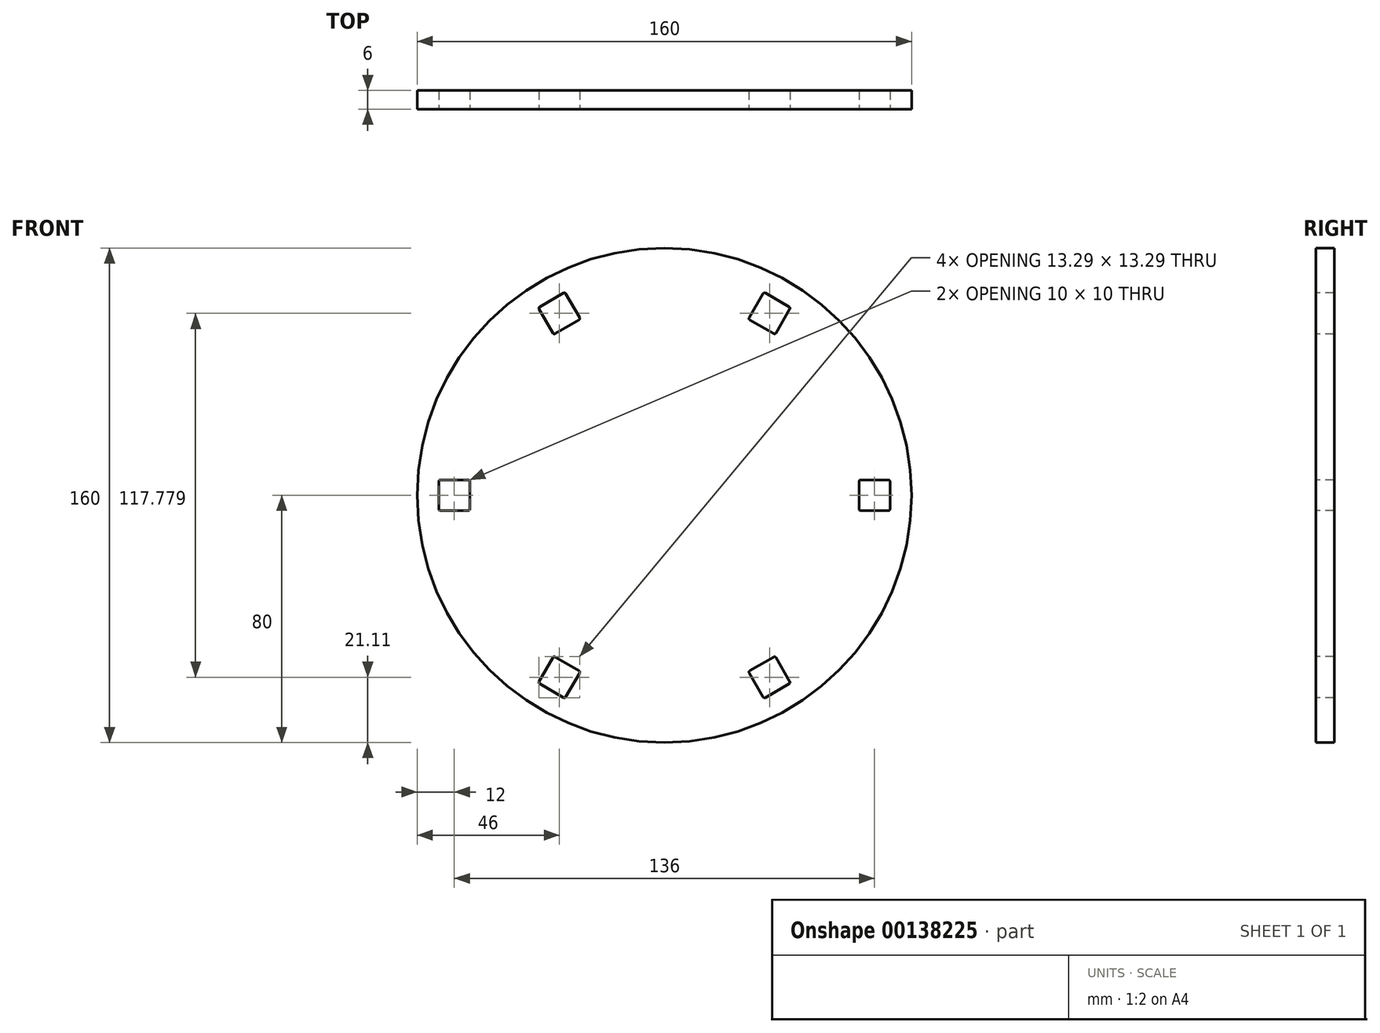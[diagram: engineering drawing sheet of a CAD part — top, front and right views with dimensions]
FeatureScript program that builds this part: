
annotation { "Feature Type Name" : "Feature", "Feature Type Description" : "" }
export const myFeature = defineFeature(function(context is Context, id is Id, definition is map)
    precondition{}
    {
        {
            var Q0;
            Q0=qCreatedBy(makeId("Front.planeOp"),FACE);
            var sketch = newSketch(context, id + "F0", { "sketchPlane" : qUnion([Q0])});
            skCircle(sketch, "E0", {"center": v(0, 0) * mm, "radius": 80 * mm});
            skCircle(sketch, "E1", {"center": v(0, 0) * mm, "radius": 56 * mm, "construction": true});
            skLineSegment(sketch, "E2", {"start": v(0, 80) * mm, "end": v(0, 56) * mm, "construction": true});
            skPoint(sketch, "E3", {"position": v(0, 68) * mm});
            skCircle(sketch, "E4", {"center": v(0, 0) * mm, "radius": 68 * mm, "construction": true});
            skLineSegment(sketch, "E5", {"start": v(-34, 58.89) * mm, "end": v(34, 58.89) * mm, "construction": true});
            skLineSegment(sketch, "E6", {"start": v(34, 58.89) * mm, "end": v(68, 0) * mm, "construction": true});
            skLineSegment(sketch, "E7", {"start": v(68, 0) * mm, "end": v(34, -58.89) * mm, "construction": true});
            skLineSegment(sketch, "E8", {"start": v(34, -58.89) * mm, "end": v(-34, -58.89) * mm, "construction": true});
            skLineSegment(sketch, "E9", {"start": v(-34, -58.89) * mm, "end": v(-68, 0) * mm, "construction": true});
            skLineSegment(sketch, "E10", {"start": v(-68, 0) * mm, "end": v(-34, 58.89) * mm, "construction": true});
            skSolve(sketch);
        }
        {
            var Q0;
            Q0 = qSketchRegion(id + "F0", true);
            extrude(context, id + "F1", {"entities" : qUnion([Q0]), "depth" : 6 * mm});
        }
        {
            var Q0;
            Q0=makeQuery(id+"F1.opExtrude","CAP_FACE",FACE,{"disambiguationData":[OSD([sQuery(id+"F0.wireOp",EDGE,"E0")])],"isStart":false});
            var sketch = newSketch(context, id + "F2", { "sketchPlane" : qUnion([Q0])});
            skLineSegment(sketch, "E11.bottom", {"start": v(-72.5, 5) * mm, "end": v(-63.5, 5) * mm});
            skLineSegment(sketch, "E11.top", {"start": v(-72.5, -5) * mm, "end": v(-63.5, -5) * mm});
            skLineSegment(sketch, "E11.left", {"start": v(-73, 4.5) * mm, "end": v(-73, -4.5) * mm});
            skLineSegment(sketch, "E11.right", {"start": v(-63, 4.5) * mm, "end": v(-63, -4.5) * mm});
            skLineSegment(sketch, "E12", {"start": v(-73, -5) * mm, "end": v(-63, 5) * mm, "construction": true});
            skLineSegment(sketch, "E13", {"start": v(-63, -5) * mm, "end": v(-73, 5) * mm, "construction": true});
            skPoint(sketch, "E14.visualSharp", {"position": v(-73, 5) * mm});
            skArc(sketch, "E14.filletArc", {"start": v(-72.5, 5) * mm, "mid": v(-72.85, 4.85) * mm, "end": v(-73, 4.5) * mm});
            skPoint(sketch, "E15.visualSharp", {"position": v(-63, 5) * mm});
            skArc(sketch, "E15.filletArc", {"start": v(-63, 4.5) * mm, "mid": v(-63.15, 4.85) * mm, "end": v(-63.5, 5) * mm});
            skPoint(sketch, "E16.visualSharp", {"position": v(-63, -5) * mm});
            skArc(sketch, "E16.filletArc", {"start": v(-63.5, -5) * mm, "mid": v(-63.15, -4.85) * mm, "end": v(-63, -4.5) * mm});
            skPoint(sketch, "E17.visualSharp", {"position": v(-73, -5) * mm});
            skArc(sketch, "E17.filletArc", {"start": v(-73, -4.5) * mm, "mid": v(-72.85, -4.85) * mm, "end": v(-72.5, -5) * mm});
            skLineSegment(sketch, "E18.1.0", {"start": v(-31.92, -65.29) * mm, "end": v(-27.42, -57.5) * mm});
            skPoint(sketch, "E18.1.1", {"position": v(-35.83, -52.06) * mm});
            skLineSegment(sketch, "E18.1.2", {"start": v(-40.4, -60.97) * mm, "end": v(-32.6, -65.47) * mm});
            skLineSegment(sketch, "E18.1.3", {"start": v(-40.58, -60.29) * mm, "end": v(-36.08, -52.5) * mm});
            skPoint(sketch, "E18.1.4", {"position": v(-40.83, -60.72) * mm});
            skPoint(sketch, "E18.1.5", {"position": v(-32.17, -65.72) * mm});
            skPoint(sketch, "E18.1.6", {"position": v(-27.17, -57.06) * mm});
            skLineSegment(sketch, "E18.1.7", {"start": v(-35.4, -52.3) * mm, "end": v(-27.6, -56.8) * mm});
            skLineSegment(sketch, "E18.1.8", {"start": v(-32.17, -65.72) * mm, "end": v(-35.83, -52.06) * mm, "construction": true});
            skLineSegment(sketch, "E18.1.9", {"start": v(-27.17, -57.06) * mm, "end": v(-40.83, -60.72) * mm, "construction": true});
            skArc(sketch, "E18.1.10", {"start": v(-32.6, -65.47) * mm, "mid": v(-32.22, -65.52) * mm, "end": v(-31.92, -65.29) * mm});
            skArc(sketch, "E18.1.11", {"start": v(-27.42, -57.5) * mm, "mid": v(-27.37, -57.11) * mm, "end": v(-27.6, -56.8) * mm});
            skArc(sketch, "E18.1.12", {"start": v(-35.4, -52.3) * mm, "mid": v(-35.78, -52.26) * mm, "end": v(-36.08, -52.5) * mm});
            skArc(sketch, "E18.1.13", {"start": v(-40.58, -60.29) * mm, "mid": v(-40.63, -60.67) * mm, "end": v(-40.4, -60.97) * mm});
            skLineSegment(sketch, "E18.2.0", {"start": v(40.58, -60.29) * mm, "end": v(36.08, -52.5) * mm});
            skPoint(sketch, "E18.2.1", {"position": v(27.17, -57.06) * mm});
            skLineSegment(sketch, "E18.2.2", {"start": v(32.6, -65.47) * mm, "end": v(40.4, -60.97) * mm});
            skLineSegment(sketch, "E18.2.3", {"start": v(31.92, -65.29) * mm, "end": v(27.42, -57.5) * mm});
            skPoint(sketch, "E18.2.4", {"position": v(32.17, -65.72) * mm});
            skPoint(sketch, "E18.2.5", {"position": v(40.83, -60.72) * mm});
            skPoint(sketch, "E18.2.6", {"position": v(35.83, -52.06) * mm});
            skLineSegment(sketch, "E18.2.7", {"start": v(27.6, -56.8) * mm, "end": v(35.4, -52.3) * mm});
            skLineSegment(sketch, "E18.2.8", {"start": v(40.83, -60.72) * mm, "end": v(27.17, -57.06) * mm, "construction": true});
            skLineSegment(sketch, "E18.2.9", {"start": v(35.83, -52.06) * mm, "end": v(32.17, -65.72) * mm, "construction": true});
            skArc(sketch, "E18.2.10", {"start": v(40.4, -60.97) * mm, "mid": v(40.63, -60.67) * mm, "end": v(40.58, -60.29) * mm});
            skArc(sketch, "E18.2.11", {"start": v(36.08, -52.5) * mm, "mid": v(35.78, -52.26) * mm, "end": v(35.4, -52.3) * mm});
            skArc(sketch, "E18.2.12", {"start": v(27.6, -56.8) * mm, "mid": v(27.37, -57.11) * mm, "end": v(27.42, -57.5) * mm});
            skArc(sketch, "E18.2.13", {"start": v(31.92, -65.29) * mm, "mid": v(32.22, -65.52) * mm, "end": v(32.6, -65.47) * mm});
            skLineSegment(sketch, "E18.3.0", {"start": v(72.5, 5) * mm, "end": v(63.5, 5) * mm});
            skPoint(sketch, "E18.3.1", {"position": v(63, -5) * mm});
            skLineSegment(sketch, "E18.3.2", {"start": v(73, -4.5) * mm, "end": v(73, 4.5) * mm});
            skLineSegment(sketch, "E18.3.3", {"start": v(72.5, -5) * mm, "end": v(63.5, -5) * mm});
            skPoint(sketch, "E18.3.4", {"position": v(73, -5) * mm});
            skPoint(sketch, "E18.3.5", {"position": v(73, 5) * mm});
            skPoint(sketch, "E18.3.6", {"position": v(63, 5) * mm});
            skLineSegment(sketch, "E18.3.7", {"start": v(63, -4.5) * mm, "end": v(63, 4.5) * mm});
            skLineSegment(sketch, "E18.3.8", {"start": v(73, 5) * mm, "end": v(63, -5) * mm, "construction": true});
            skLineSegment(sketch, "E18.3.9", {"start": v(63, 5) * mm, "end": v(73, -5) * mm, "construction": true});
            skArc(sketch, "E18.3.10", {"start": v(73, 4.5) * mm, "mid": v(72.85, 4.85) * mm, "end": v(72.5, 5) * mm});
            skArc(sketch, "E18.3.11", {"start": v(63.5, 5) * mm, "mid": v(63.15, 4.85) * mm, "end": v(63, 4.5) * mm});
            skArc(sketch, "E18.3.12", {"start": v(63, -4.5) * mm, "mid": v(63.15, -4.85) * mm, "end": v(63.5, -5) * mm});
            skArc(sketch, "E18.3.13", {"start": v(72.5, -5) * mm, "mid": v(72.85, -4.85) * mm, "end": v(73, -4.5) * mm});
            skLineSegment(sketch, "E18.4.0", {"start": v(31.92, 65.29) * mm, "end": v(27.42, 57.5) * mm});
            skPoint(sketch, "E18.4.1", {"position": v(35.83, 52.06) * mm});
            skLineSegment(sketch, "E18.4.2", {"start": v(40.4, 60.97) * mm, "end": v(32.6, 65.47) * mm});
            skLineSegment(sketch, "E18.4.3", {"start": v(40.58, 60.29) * mm, "end": v(36.08, 52.5) * mm});
            skPoint(sketch, "E18.4.4", {"position": v(40.83, 60.72) * mm});
            skPoint(sketch, "E18.4.5", {"position": v(32.17, 65.72) * mm});
            skPoint(sketch, "E18.4.6", {"position": v(27.17, 57.06) * mm});
            skLineSegment(sketch, "E18.4.7", {"start": v(35.4, 52.3) * mm, "end": v(27.6, 56.8) * mm});
            skLineSegment(sketch, "E18.4.8", {"start": v(32.17, 65.72) * mm, "end": v(35.83, 52.06) * mm, "construction": true});
            skLineSegment(sketch, "E18.4.9", {"start": v(27.17, 57.06) * mm, "end": v(40.83, 60.72) * mm, "construction": true});
            skArc(sketch, "E18.4.10", {"start": v(32.6, 65.47) * mm, "mid": v(32.22, 65.52) * mm, "end": v(31.92, 65.29) * mm});
            skArc(sketch, "E18.4.11", {"start": v(27.42, 57.5) * mm, "mid": v(27.37, 57.11) * mm, "end": v(27.6, 56.8) * mm});
            skArc(sketch, "E18.4.12", {"start": v(35.4, 52.3) * mm, "mid": v(35.78, 52.26) * mm, "end": v(36.08, 52.5) * mm});
            skArc(sketch, "E18.4.13", {"start": v(40.58, 60.29) * mm, "mid": v(40.63, 60.67) * mm, "end": v(40.4, 60.97) * mm});
            skLineSegment(sketch, "E18.5.0", {"start": v(-40.58, 60.29) * mm, "end": v(-36.08, 52.5) * mm});
            skPoint(sketch, "E18.5.1", {"position": v(-27.17, 57.06) * mm});
            skLineSegment(sketch, "E18.5.2", {"start": v(-32.6, 65.47) * mm, "end": v(-40.4, 60.97) * mm});
            skLineSegment(sketch, "E18.5.3", {"start": v(-31.92, 65.29) * mm, "end": v(-27.42, 57.5) * mm});
            skPoint(sketch, "E18.5.4", {"position": v(-32.17, 65.72) * mm});
            skPoint(sketch, "E18.5.5", {"position": v(-40.83, 60.72) * mm});
            skPoint(sketch, "E18.5.6", {"position": v(-35.83, 52.06) * mm});
            skLineSegment(sketch, "E18.5.7", {"start": v(-27.6, 56.8) * mm, "end": v(-35.4, 52.3) * mm});
            skLineSegment(sketch, "E18.5.8", {"start": v(-40.83, 60.72) * mm, "end": v(-27.17, 57.06) * mm, "construction": true});
            skLineSegment(sketch, "E18.5.9", {"start": v(-35.83, 52.06) * mm, "end": v(-32.17, 65.72) * mm, "construction": true});
            skArc(sketch, "E18.5.10", {"start": v(-40.4, 60.97) * mm, "mid": v(-40.63, 60.67) * mm, "end": v(-40.58, 60.29) * mm});
            skArc(sketch, "E18.5.11", {"start": v(-36.08, 52.5) * mm, "mid": v(-35.78, 52.26) * mm, "end": v(-35.4, 52.3) * mm});
            skArc(sketch, "E18.5.12", {"start": v(-27.6, 56.8) * mm, "mid": v(-27.37, 57.11) * mm, "end": v(-27.42, 57.5) * mm});
            skArc(sketch, "E18.5.13", {"start": v(-31.92, 65.29) * mm, "mid": v(-32.22, 65.52) * mm, "end": v(-32.6, 65.47) * mm});
            skPoint(sketch, "E18.center", {"position": v(0, 0) * mm});
            skSolve(sketch);
        }
        {
            var Q0;
            Q0 = qSketchRegion(id + "F2", true);
            extrude(context, id + "F3", {"entities" : qUnion([Q0]), "operationType" : NewBodyOperationType.REMOVE, "endBound" : BoundingType.THROUGH_ALL, "oppositeDirection" : true, "depth" : 25 * mm});
        }
    });
